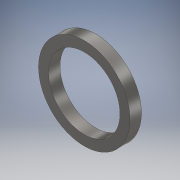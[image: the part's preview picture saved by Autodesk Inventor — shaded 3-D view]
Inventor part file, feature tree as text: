
AUTODESK INVENTOR PART (.ipt)
format: ipt  version: 2018 (Build 220112000, 112)  size: 104,960 bytes
history: native  units: mm
features: extrude x1, sketch x1
ambient origin geometry x8: Origin, YZ Plane, XZ Plane, XY Plane, X Axis, Y Axis, Z Axis, Center Point
bodies: Solid1 (feature_tree)
feature tree (2):
  extrude  "Extrusion1"  Depth=4.0mm
  sketch  "Sketch1"  dims[d0=25.0mm d1=32.0mm d2=4.0mm d3=0.0mm]
